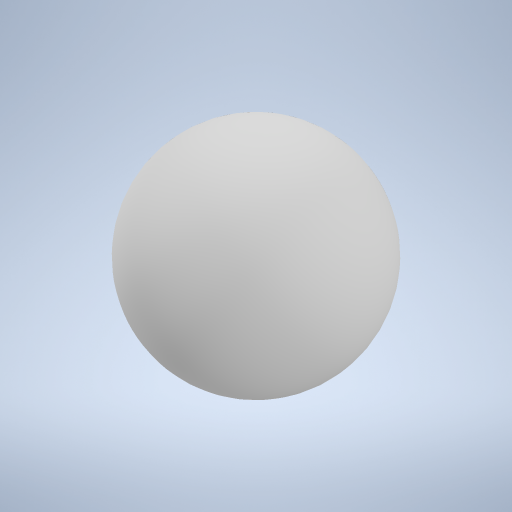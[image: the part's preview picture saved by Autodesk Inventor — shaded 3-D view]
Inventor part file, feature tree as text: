
AUTODESK INVENTOR PART (.ipt)
format: ipt  version: 2023 (Build 270158000, 158)  size: 243,712 bytes
history: native  units: mm
features: other x2, sketch x1
ambient origin geometry x8: Origin, YZ Plane, XZ Plane, XY Plane, X Axis, Y Axis, Z Axis, Center Point
bodies: Body1 (feature_tree)
feature tree (3):
  other  "Sólido1"
  other  "Revolução1"
  sketch  "Esboço1"  dims[d0=49.5mm d1=90.0deg]
